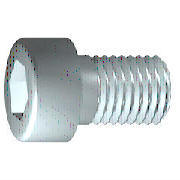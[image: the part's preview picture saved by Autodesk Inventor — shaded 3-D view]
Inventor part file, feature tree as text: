
AUTODESK INVENTOR PART (.ipt)
format: ipt  version: 2020 (Build 240168000, 168)  size: 189,952 bytes
history: native  units: mm (DEFAULTED — no unit token found)
features: sketch x2, other x1, extrude x1, plane x1, fillet x1
ambient origin geometry x7: Origin, YZ Plane, XY Plane, X Axis, Y Axis, Z Axis, Center Point
bodies: Solid1 (feature_tree)
feature tree (6):
  other  "Bryła"
  extrude  "Szczelina"  Depth=23.25mm
  plane  "Work Plane1"
  fillet  "Fillet2"  Radius=0.429515mm
  sketch  "Szkic1"
  sketch  "Szkic2"
